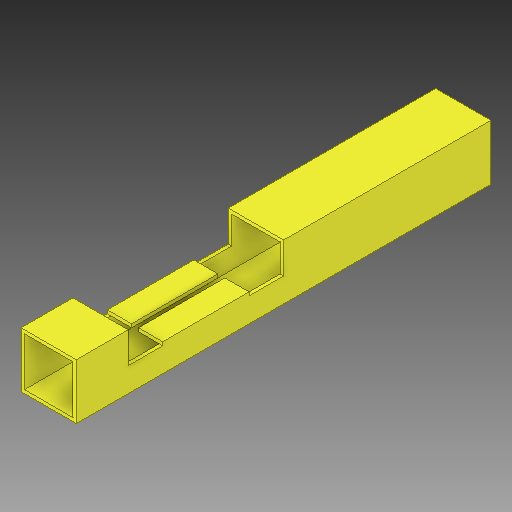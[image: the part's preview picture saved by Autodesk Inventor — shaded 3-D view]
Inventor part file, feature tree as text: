
AUTODESK INVENTOR PART (.ipt)
format: ipt  version: 2019 (Build 230136000, 136)  size: 104,448 bytes
history: native  units: in
note: dims shown in document units (in); Inventor stores cm internally (conversion verified against a paired STEP export)
features: mirror x1
ambient origin geometry x8: Origin, YZ Plane, XZ Plane, XY Plane, X Axis, Y Axis, Z Axis, Center Point
bodies: Solid1 (feature_tree)
feature tree (1):
  mirror  "Mirror1"
